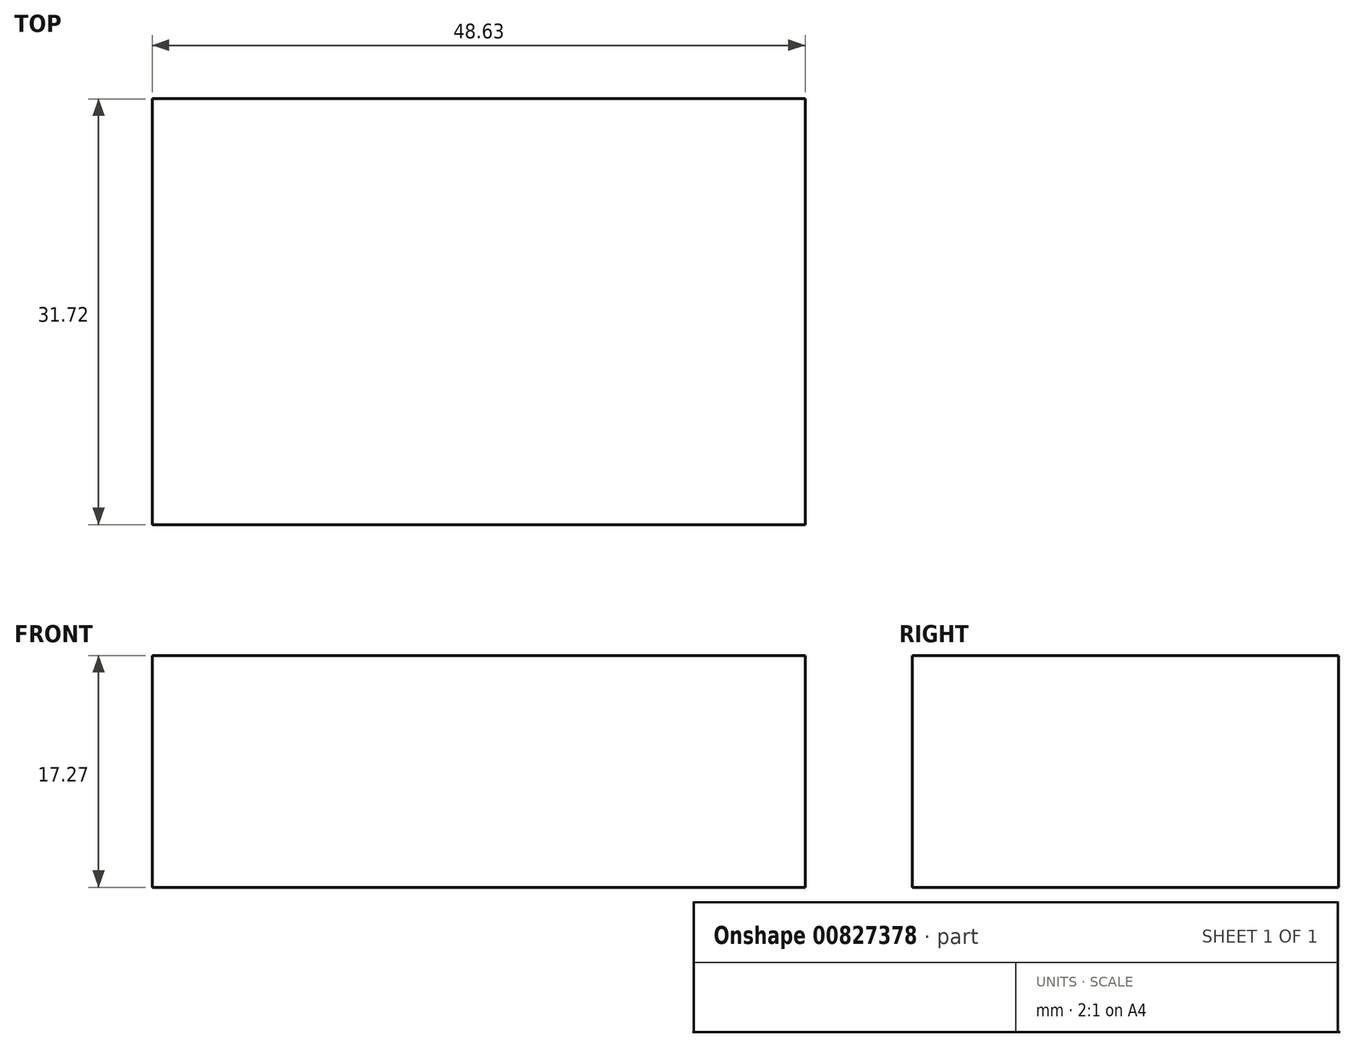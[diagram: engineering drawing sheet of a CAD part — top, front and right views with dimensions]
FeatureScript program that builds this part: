
annotation { "Feature Type Name" : "Feature", "Feature Type Description" : "" }
export const myFeature = defineFeature(function(context is Context, id is Id, definition is map)
    precondition{}
    {
        {
            var Q0;
            Q0=qCreatedBy(makeId("Top.planeOp"),FACE);
            var sketch = newSketch(context, id + "F0", { "sketchPlane" : qUnion([Q0])});
            skLineSegment(sketch, "E0.bottom", {"start": v(-62.47, 44.93) * mm, "end": v(-13.84, 44.93) * mm});
            skLineSegment(sketch, "E0.top", {"start": v(-62.47, 13.2) * mm, "end": v(-13.84, 13.2) * mm});
            skLineSegment(sketch, "E0.left", {"start": v(-62.47, 44.93) * mm, "end": v(-62.47, 13.2) * mm});
            skLineSegment(sketch, "E0.right", {"start": v(-13.84, 44.93) * mm, "end": v(-13.84, 13.2) * mm});
            skSolve(sketch);
        }
        {
            var Q0;
            Q0 = qSketchRegion(id + "F0", true);
            extrude(context, id + "F1", {"entities" : qUnion([Q0]), "depth" : 17.27 * mm, "offsetDistance" : 25.4 * mm});
        }
    });
